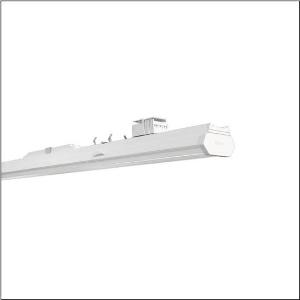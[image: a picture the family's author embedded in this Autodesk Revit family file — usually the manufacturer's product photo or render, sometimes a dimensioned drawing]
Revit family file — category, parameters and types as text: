
# Revit family: licross_r__11_protected_ho_51td12dn4fxm_db4e
name_source: partatom
category: Lighting Fixtures
units: mm (PartAtom-declared; Revit-internal decimal feet)

## family parameters
Cut with Voids When Loaded = No
Host = Face
Light Source = No
Part Type = Normal
Room Calculation Point = No
Round Connector Dimension = Use Diameter
Shared = No

## types (1)
- --- (1 x LED, 15270 lm, 87.3 W, 4000K)
    Apparent Load = 87 VA
    CIE Flux Codes = 70 91 97 98 100
    Color Rendering = 80
    Color Temperature = 4000K
    Default Elevation = 1800 mm
    Description = Licross® 11 Protected HO, luminaire insert, of sheet steel, galvanised, coil coated, white, length: 1.500mm, width: 90mm, height: 101mm, LED rated luminous flux: 15.270lm, light colour: 840, control gear: DALI 2, with plug, 5-pole, with phase selection, mains connection: 220..240V, AC, 50/60Hz, rated input power: 87W, halogen-free wiring, primary optical cover: cover, of PMMA, light emission: direct distribution, primary light characteristic: symmetric, protection rating (complete): IP54, insulation class (complete): insulation class I (protective earthing), certification: CE, ENEC, VDE, UKCA, protection symbol: D if used in an environment with non-conductive dust loads with corresponding accessories, impact resistance: IK06, permissible ambient temperature for indoor applications: -25..+30°C, corresponds to IFS (International Featured Standards) requirements for safety and quality in the food industry, reducing of maximum allowable ambient temperature of 5°C with ceiling mounting, LABS conformity tested according to VDMA 24364:2018-05, packaging unit: 1 piece
    Height = 92 mm
    Lamp = 1 x LED
    Lamp Light Flux = 15270 lm
    Lamp Power = 87.3 W
    Lamp count = 1
    Length = 1500 mm
    Luminous efficacy = 175 lm/W
    Manufacturer = Siteco
    ModVariant = No
    Model = 51TD12DN4FXM
    Mounting Place = Ceiling
    Mounting Type = Pendant
    Number of Poles = 1
    OnlyDefault = Yes
    Power Factor = 1
    Product Name = Licross® 11 Protected HO
    Product group = luminaire insert
    ProductGroupID = 901
    Protection Class = Protection class I
    Protection Degree = IP 54
    RLX_Detail_Level = 1
    RLX_Emergency_Light_Flux = 0 lm
    RLX_Emergency_Type = 0
    RLX_Emergency_Type_DB = No
    RlxData = <blob elided: 24309 chars, md5=bdac483d>
    Socket = socket
    Standby Power = 0 W
    System Light Flux = 15270 lm
    System Power = 87 W
    Type Comments = factory setting: luminous flux: 100 % | dim-lin: 254 | 589 mA
    Type Image = l_1256145.jpg
    URL = http://relux.com
    VarID = @adj_031309
    Voltage = 0 V
    Weight = 0.00 kg
    Width = 88 mm

## geometry (parser evidence)
native form markers: Blend x4, Sweep x8
no freeform markers — native parametric forms only
